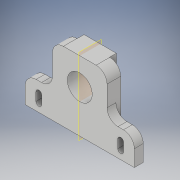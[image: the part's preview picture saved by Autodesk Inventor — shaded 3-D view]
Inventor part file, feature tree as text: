
AUTODESK INVENTOR PART (.ipt)
format: ipt  version: 2018 (Build 220112000, 112)  size: 175,104 bytes
history: native  units: in
note: dims shown in document units (in); Inventor stores cm internally (conversion verified against a paired STEP export)
features: extrude x5, sketch x5, fillet x1, mirror x1
ambient origin geometry x8: Origin, YZ Plane, XZ Plane, XY Plane, X Axis, Y Axis, Z Axis, Center Point
bodies: Solid1 (feature_tree)
feature tree (12):
  extrude  "Extrusion1"  Depth=0.7874in
  sketch  "Sketch2"  dims[d2=1.5748in d3=1.2205in]
  extrude  "Extrusion2"  Depth=1.2205in
  extrude  "Extrusion3"  Depth=0.2559in
  extrude  "Extrusion4"  Depth=0.7874in
  fillet  "Fillet1"  Radius=0.7185in
  extrude  "Extrusion5"  Depth=0.9331in
  mirror  "Mirror1"
  sketch  "Sketch1"  dims[d0=3.1496in d1=0.7874in]
  sketch  "Sketch3"  dims[d4=0.2559in d5=0.0in d6=0.7185in]
  sketch  "Sketch4"  dims[d7=0.7874in d8=0.7874in d9=0.7185in]
  sketch  "Sketch5"  dims[d10=0.1378in d11=0.0in d12=0.9331in d13=0.1969in d14=0.0in d15=0.1969in d16=0.0in d17=0.315in d18=0.1654in d19=0.2409in d20=0.3937in d21=0.2362in d22=0.1969in d23=0.0in]
